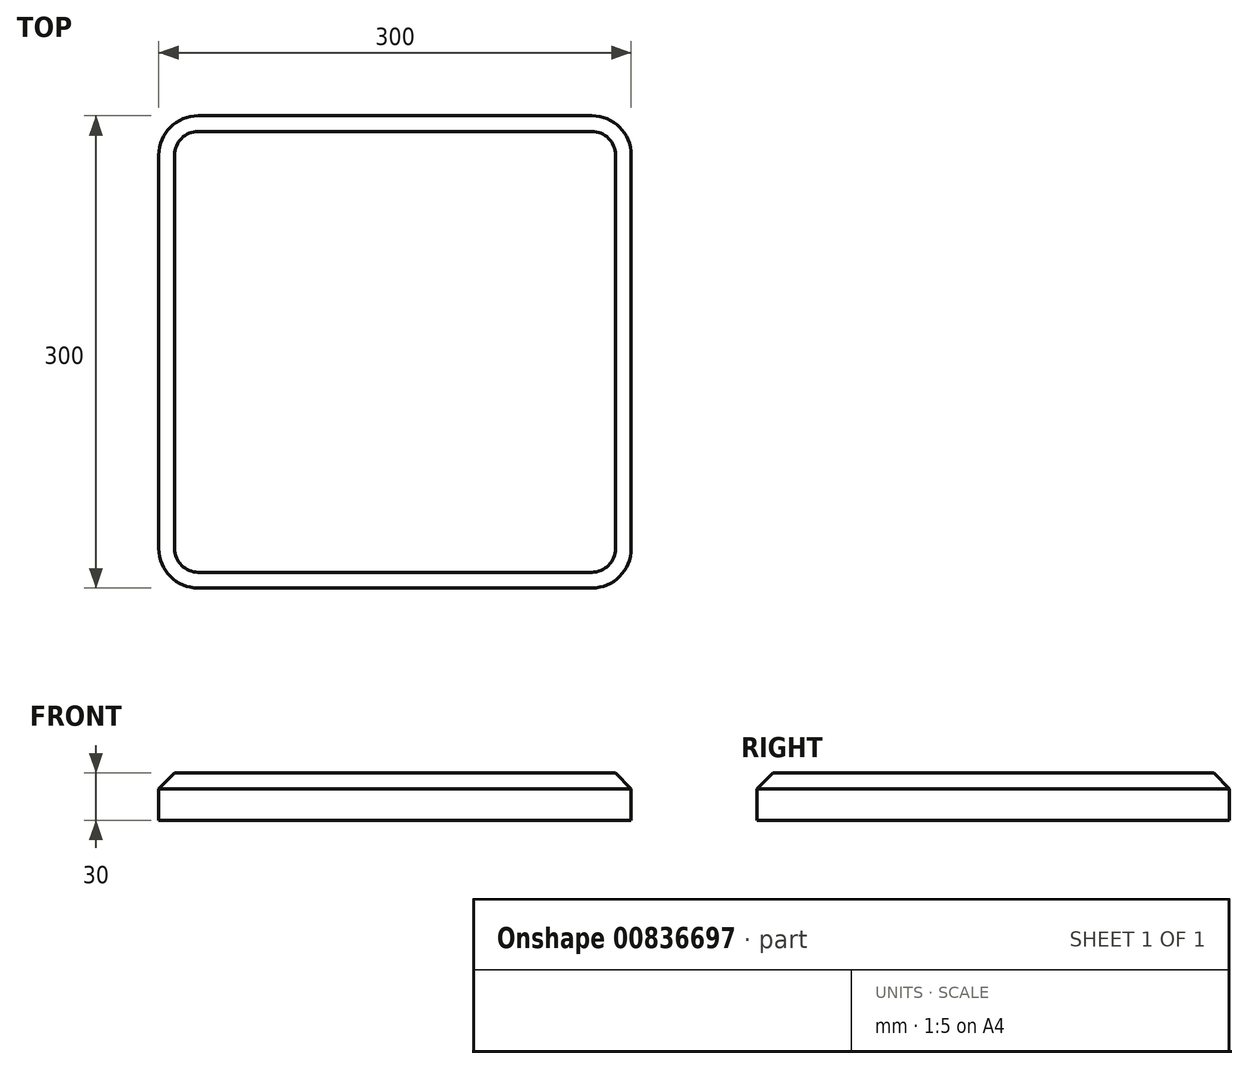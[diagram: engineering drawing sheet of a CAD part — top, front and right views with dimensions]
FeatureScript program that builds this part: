
annotation { "Feature Type Name" : "Feature", "Feature Type Description" : "" }
export const myFeature = defineFeature(function(context is Context, id is Id, definition is map)
    precondition{}
    {
        {
            var Q0;
            Q0=qCreatedBy(makeId("Top.planeOp"),FACE);
            var sketch = newSketch(context, id + "F0", { "sketchPlane" : qUnion([Q0])});
            skLineSegment(sketch, "E0.bottom", {"start": v(0, 0) * mm, "end": v(-150, 0) * mm, "construction": true});
            skLineSegment(sketch, "E0.top", {"start": v(0, 150) * mm, "end": v(-125, 150) * mm});
            skLineSegment(sketch, "E0.left", {"start": v(0, 0) * mm, "end": v(0, 150) * mm, "construction": true});
            skLineSegment(sketch, "E0.right", {"start": v(-150, 0) * mm, "end": v(-150, 125) * mm});
            skArc(sketch, "E1", {"start": v(-125, 150) * mm, "mid": v(-142.68, 142.68) * mm, "end": v(-150, 125) * mm});
            skLineSegment(sketch, "E2.MirrorCS", {"start": v(0, 150) * mm, "end": v(125, 150) * mm});
            skLineSegment(sketch, "E3.MirrorCS", {"start": v(0, 0) * mm, "end": v(150, 0) * mm, "construction": true});
            skLineSegment(sketch, "E4.MirrorCS", {"start": v(150, 0) * mm, "end": v(150, 125) * mm});
            skArc(sketch, "E5.MirrorCS", {"start": v(125, 150) * mm, "mid": v(142.68, 142.68) * mm, "end": v(150, 125) * mm});
            skLineSegment(sketch, "E6.MirrorCS", {"start": v(0, 0) * mm, "end": v(0, -150) * mm, "construction": true});
            skArc(sketch, "E7.MirrorCS", {"start": v(125, -150) * mm, "mid": v(142.68, -142.68) * mm, "end": v(150, -125) * mm});
            skArc(sketch, "E8.MirrorCS", {"start": v(-125, -150) * mm, "mid": v(-142.68, -142.68) * mm, "end": v(-150, -125) * mm});
            skLineSegment(sketch, "E9.MirrorCS", {"start": v(0, -150) * mm, "end": v(-125, -150) * mm});
            skLineSegment(sketch, "E10.MirrorCS", {"start": v(-150, 0) * mm, "end": v(-150, -125) * mm});
            skLineSegment(sketch, "E11.MirrorCS", {"start": v(0, -150) * mm, "end": v(125, -150) * mm});
            skLineSegment(sketch, "E12.MirrorCS", {"start": v(150, 0) * mm, "end": v(150, -125) * mm});
            skSolve(sketch);
        }
        {
            var Q0;
            Q0 = qSketchRegion(id + "F0", true);
            extrude(context, id + "F1", {"entities" : qUnion([Q0]), "depth" : 30 * mm, "offsetDistance" : 25 * mm});
        }
        {
            var Q0;
            Q0=makeQuery(id+"F1.opExtrude","CAP_EDGE",EDGE,{"disambiguationData":[OSD([sQuery(id+"F0.wireOp",EDGE,"E0.top"),sQuery(id+"F0.wireOp",EDGE,"E2.MirrorCS")])],"isStart":false});
            chamfer(context, id + "F2", {"entities" : qUnion([Q0]), "width" : 10 * mm, "tangentPropagation" : true});
        }
    });
